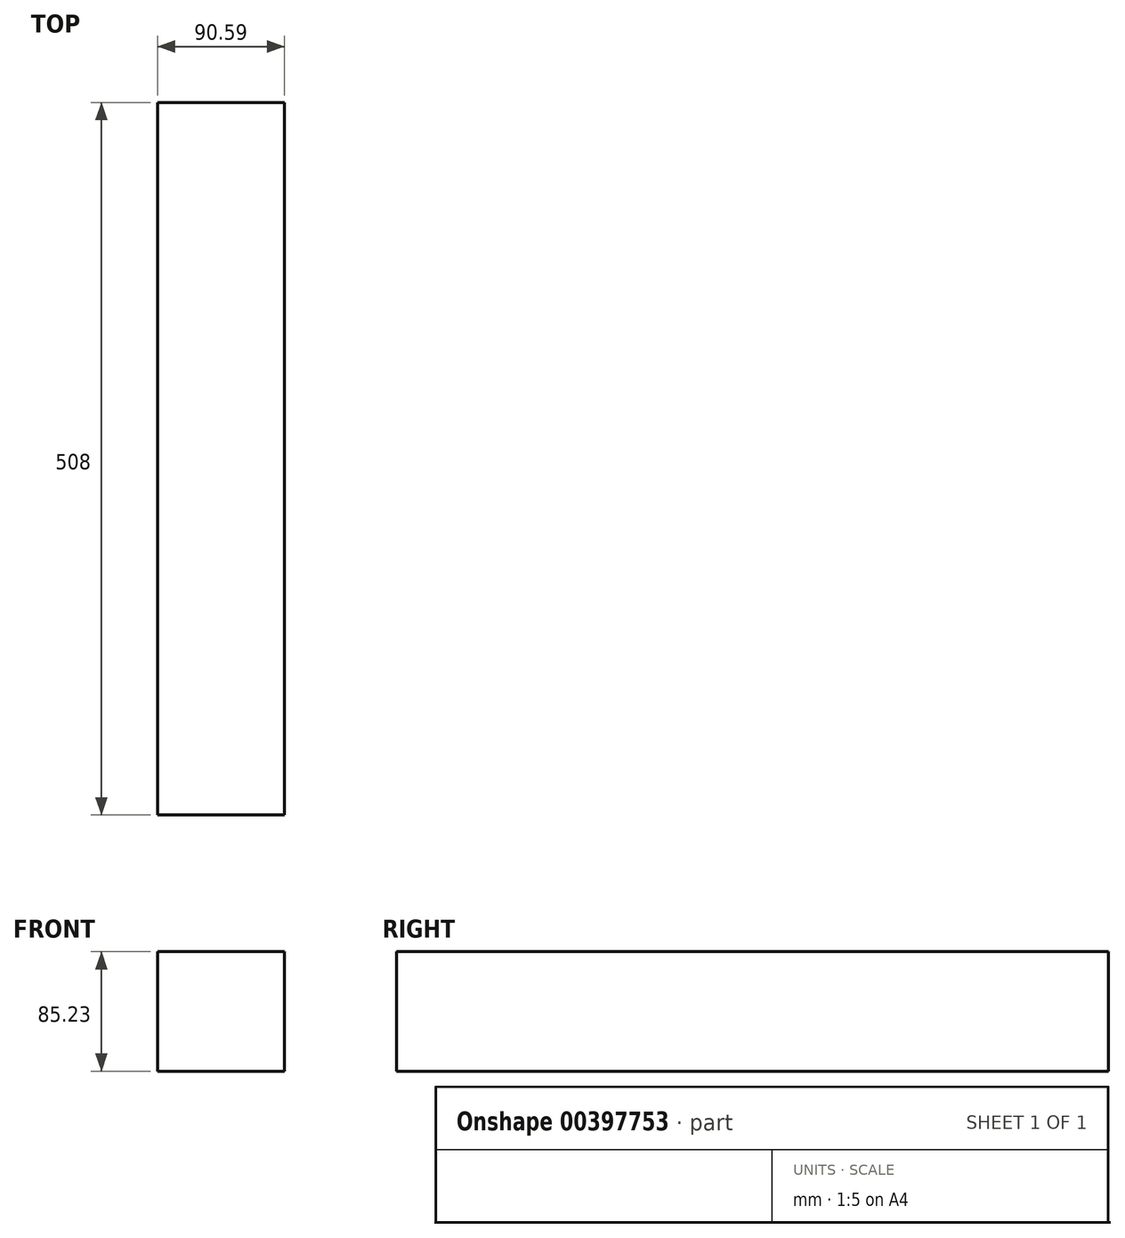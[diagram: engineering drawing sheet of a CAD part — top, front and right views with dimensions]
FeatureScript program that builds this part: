
annotation { "Feature Type Name" : "Feature", "Feature Type Description" : "" }
export const myFeature = defineFeature(function(context is Context, id is Id, definition is map)
    precondition{}
    {
        {
            var Q0;
            Q0=qCreatedBy(makeId("Front.planeOp"),FACE);
            var sketch = newSketch(context, id + "F0", { "sketchPlane" : qUnion([Q0])});
            skLineSegment(sketch, "E0.bottom", {"start": v(0, 0) * mm, "end": v(90.59, 0) * mm});
            skLineSegment(sketch, "E0.top", {"start": v(0, -85.23) * mm, "end": v(90.59, -85.23) * mm});
            skLineSegment(sketch, "E0.left", {"start": v(0, 0) * mm, "end": v(0, -85.23) * mm});
            skLineSegment(sketch, "E0.right", {"start": v(90.59, 0) * mm, "end": v(90.59, -85.23) * mm});
            skSolve(sketch);
        }
        {
            var Q0;
            Q0=makeQuery(id+"F0.imprint","IMPRINT",FACE,{"disambiguationData":[TD([[makeQuery(id+"F0.imprint","IMPRINT",EDGE,{"derivedFrom":sQuery(id+"F0.wireOp",EDGE,"E0.bottom")}),-1.0]])]});
            extrude(context, id + "F1", {"entities" : qUnion([Q0]), "oppositeDirection" : true, "depth" : 508 * mm});
        }
    });
